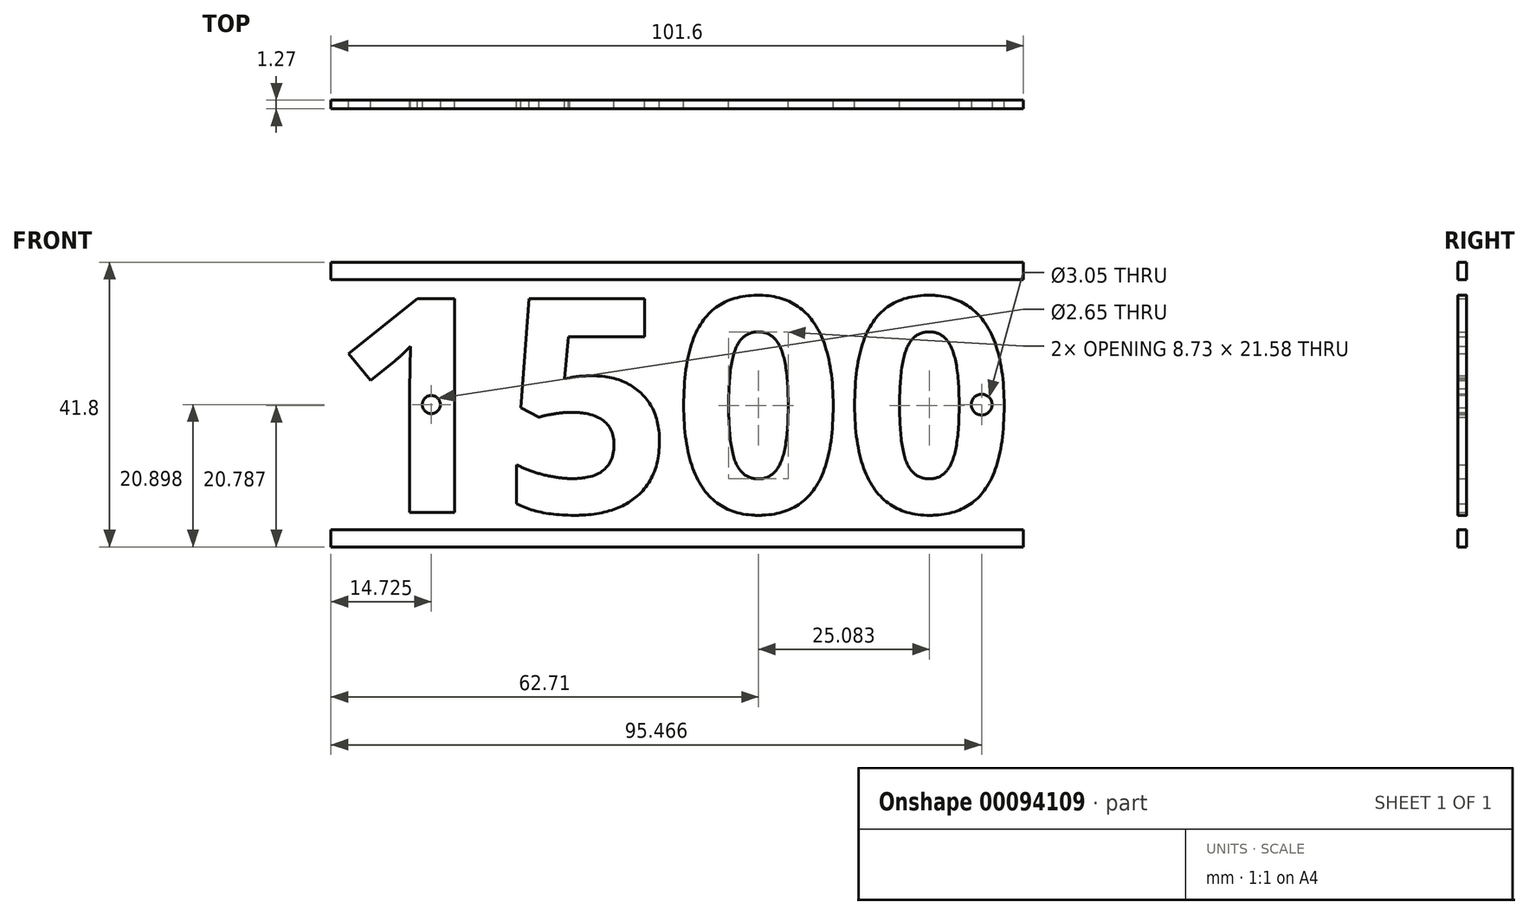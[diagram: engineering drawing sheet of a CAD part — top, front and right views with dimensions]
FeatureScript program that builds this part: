
annotation { "Feature Type Name" : "Feature", "Feature Type Description" : "" }
export const myFeature = defineFeature(function(context is Context, id is Id, definition is map)
    precondition{}
    {
        {
            var Q0;
            Q0=qCreatedBy(makeId("Front.planeOp"),FACE);
            var sketch = newSketch(context, id + "F0", { "sketchPlane" : qUnion([Q0])});
            skText(sketch, "E0", { "text": "1500", "fontName": "OpenSans-Bold.ttf"});
            skLineSegment(sketch, "E1.bottom", {"start": v(0, -2.54) * mm, "end": v(101.6, -2.54) * mm});
            skLineSegment(sketch, "E1.top", {"start": v(0, -5.08) * mm, "end": v(101.6, -5.08) * mm});
            skLineSegment(sketch, "E1.left", {"start": v(0, -2.54) * mm, "end": v(0, -5.08) * mm});
            skLineSegment(sketch, "E1.right", {"start": v(101.6, -2.54) * mm, "end": v(101.6, -5.08) * mm});
            skLineSegment(sketch, "E2.bottom", {"start": v(0, 36.72) * mm, "end": v(101.6, 36.72) * mm});
            skLineSegment(sketch, "E2.top", {"start": v(0, 34.18) * mm, "end": v(101.6, 34.18) * mm});
            skLineSegment(sketch, "E2.left", {"start": v(0, 36.72) * mm, "end": v(0, 34.18) * mm});
            skLineSegment(sketch, "E2.right", {"start": v(101.6, 36.72) * mm, "end": v(101.6, 34.18) * mm});
            skLineSegment(sketch, "E3.bottom", {"start": v(14.13, 34.18) * mm, "end": v(15.4, 34.18) * mm});
            skLineSegment(sketch, "E3.top", {"start": v(14.13, -2.54) * mm, "end": v(15.4, -2.54) * mm});
            skLineSegment(sketch, "E3.left", {"start": v(14.13, 34.18) * mm, "end": v(14.13, -2.54) * mm});
            skLineSegment(sketch, "E3.right", {"start": v(15.4, 34.18) * mm, "end": v(15.4, -2.54) * mm});
            skLineSegment(sketch, "E4.bottom", {"start": v(36.1, 34.18) * mm, "end": v(37.37, 34.18) * mm});
            skLineSegment(sketch, "E4.top", {"start": v(36.1, -2.54) * mm, "end": v(37.37, -2.54) * mm});
            skLineSegment(sketch, "E4.left", {"start": v(36.1, 34.18) * mm, "end": v(36.1, -2.54) * mm});
            skLineSegment(sketch, "E4.right", {"start": v(37.37, 34.18) * mm, "end": v(37.37, -2.54) * mm});
            skLineSegment(sketch, "E5.bottom", {"start": v(62.1, 34.18) * mm, "end": v(63.38, 34.18) * mm});
            skLineSegment(sketch, "E5.top", {"start": v(62.1, -2.54) * mm, "end": v(63.38, -2.54) * mm});
            skLineSegment(sketch, "E5.left", {"start": v(62.1, 34.18) * mm, "end": v(62.1, -2.54) * mm});
            skLineSegment(sketch, "E5.right", {"start": v(63.38, 34.18) * mm, "end": v(63.38, -2.54) * mm});
            skLineSegment(sketch, "E6.bottom", {"start": v(87.42, 34.18) * mm, "end": v(88.69, 34.18) * mm});
            skLineSegment(sketch, "E6.top", {"start": v(87.42, -2.54) * mm, "end": v(88.69, -2.54) * mm});
            skLineSegment(sketch, "E6.left", {"start": v(87.42, 34.18) * mm, "end": v(87.42, -2.54) * mm});
            skLineSegment(sketch, "E6.right", {"start": v(88.69, 34.18) * mm, "end": v(88.69, -2.54) * mm});
            skLineSegment(sketch, "E7", {"start": v(36.1, 29.2) * mm, "end": v(37.37, 29.2) * mm});
            skLineSegment(sketch, "E8", {"start": v(36.1, 2.08) * mm, "end": v(37.37, 2.08) * mm});
            skLineSegment(sketch, "E9", {"start": v(62.1, 2.01) * mm, "end": v(63.38, 2.01) * mm});
            skLineSegment(sketch, "E10", {"start": v(62.1, 29.7) * mm, "end": v(63.38, 29.7) * mm});
            skLineSegment(sketch, "E11", {"start": v(87.42, 2.66) * mm, "end": v(88.69, 2.66) * mm});
            skLineSegment(sketch, "E12", {"start": v(87.42, 27.18) * mm, "end": v(88.69, 27.18) * mm});
            const initialGuessF0  = {"E0": [0, 0, 1, 0, 0.03164]};
            skSetInitialGuess(sketch, initialGuessF0);
            skSolve(sketch);
        }
        {
            var Q0;
            Q0=makeQuery(id+"F0.imprint","IMPRINT",FACE,{"disambiguationData":[TD([[makeQuery(id+"F0.imprint","IMPRINT",EDGE,{"derivedFrom":sQuery(id+"F0.wireOp",EDGE,"E2.bottom")}),-1.0]])]});
            var Q1;
            {var subQ5=sQuery(id+"F0.wireOp",EDGE,"E3.bottom");Q1=makeQuery(id+"F0.imprint","IMPRINT",FACE,{"disambiguationData":[TD([[makeQuery(id+"F0.imprint","IMPRINT",EDGE,{"derivedFrom":subQ5}),-1.0]])]});}
            var Q2;
            {var subQ0=sQuery(id+"F0.wireOp",EDGE,"E3.left");var subQ1=sQuery(id+"F0.wireOp",EDGE,"E0.sketch_text.stroke-0");var subQ2=makeQuery(id+"F0.imprint","INTERSECT",VERTEX,{"derivedFrom":[subQ1,subQ0]});Q2=makeQuery(id+"F0.imprint","IMPRINT",FACE,{"disambiguationData":[TD([[makeQuery(id+"F0.imprint","IMPRINT",EDGE,{"disambiguationData":[TD([[subQ2,1.0]])],"derivedFrom":subQ1}),-1.0]])]});}
            var Q3;
            {var subQ0=sQuery(id+"F0.wireOp",EDGE,"E0.sketch_text.stroke-9");Q3=makeQuery(id+"F0.imprint","IMPRINT",FACE,{"disambiguationData":[TD([[makeQuery(id+"F0.imprint","IMPRINT",EDGE,{"derivedFrom":subQ0}),-1.0]])]});}
            var Q4;
            {var subQ0=sQuery(id+"F0.wireOp",EDGE,"E0.sketch_text.stroke-1");Q4=makeQuery(id+"F0.imprint","IMPRINT",FACE,{"disambiguationData":[TD([[makeQuery(id+"F0.imprint","IMPRINT",EDGE,{"derivedFrom":subQ0}),-1.0]])]});}
            var Q5;
            {var subQ5=sQuery(id+"F0.wireOp",EDGE,"E3.top");Q5=makeQuery(id+"F0.imprint","IMPRINT",FACE,{"disambiguationData":[TD([[makeQuery(id+"F0.imprint","IMPRINT",EDGE,{"derivedFrom":subQ5}),1.0]])]});}
            var Q6;
            Q6=makeQuery(id+"F0.imprint","IMPRINT",FACE,{"disambiguationData":[TD([[makeQuery(id+"F0.imprint","IMPRINT",EDGE,{"derivedFrom":sQuery(id+"F0.wireOp",EDGE,"E1.top")}),1.0]])]});
            var Q7;
            {var subQ5=sQuery(id+"F0.wireOp",EDGE,"E4.top");Q7=makeQuery(id+"F0.imprint","IMPRINT",FACE,{"disambiguationData":[TD([[makeQuery(id+"F0.imprint","IMPRINT",EDGE,{"derivedFrom":subQ5}),1.0]])]});}
            var Q8;
            {var subQ9=sQuery(id+"F0.wireOp",EDGE,"E0.sketch_text.stroke-10");Q8=makeQuery(id+"F0.imprint","IMPRINT",FACE,{"disambiguationData":[TD([[makeQuery(id+"F0.imprint","IMPRINT",EDGE,{"derivedFrom":subQ9}),-1.0]])]});}
            var Q9;
            {var subQ1=sQuery(id+"F0.wireOp",EDGE,"E0.sketch_text.stroke-14");Q9=makeQuery(id+"F0.imprint","IMPRINT",FACE,{"disambiguationData":[TD([[makeQuery(id+"F0.imprint","IMPRINT",EDGE,{"derivedFrom":subQ1}),-1.0]])]});}
            var Q10;
            {var subQ5=sQuery(id+"F0.wireOp",EDGE,"E8");Q10=makeQuery(id+"F0.imprint","IMPRINT",FACE,{"disambiguationData":[TD([[makeQuery(id+"F0.imprint","IMPRINT",EDGE,{"derivedFrom":subQ5}),1.0]])]});}
            var Q11;
            {var subQ5=sQuery(id+"F0.wireOp",EDGE,"E8");Q11=makeQuery(id+"F0.imprint","IMPRINT",FACE,{"disambiguationData":[TD([[makeQuery(id+"F0.imprint","IMPRINT",EDGE,{"derivedFrom":subQ5}),-1.0]])]});}
            var Q12;
            {var subQ0=sQuery(id+"F0.wireOp",EDGE,"E4.right");var subQ1=sQuery(id+"F0.wireOp",EDGE,"E0.sketch_text.stroke-19");var subQ2=makeQuery(id+"F0.imprint","INTERSECT",VERTEX,{"derivedFrom":[subQ1,subQ0]});Q12=makeQuery(id+"F0.imprint","IMPRINT",FACE,{"disambiguationData":[TD([[makeQuery(id+"F0.imprint","IMPRINT",EDGE,{"disambiguationData":[TD([[subQ2,-1.0]])],"derivedFrom":subQ1}),-1.0]])]});}
            var Q13;
            {var subQ10=sQuery(id+"F0.wireOp",EDGE,"E0.sketch_text.stroke-20");Q13=makeQuery(id+"F0.imprint","IMPRINT",FACE,{"disambiguationData":[TD([[makeQuery(id+"F0.imprint","IMPRINT",EDGE,{"derivedFrom":subQ10}),-1.0]])]});}
            var Q14;
            {var subQ5=sQuery(id+"F0.wireOp",EDGE,"E7");Q14=makeQuery(id+"F0.imprint","IMPRINT",FACE,{"disambiguationData":[TD([[makeQuery(id+"F0.imprint","IMPRINT",EDGE,{"derivedFrom":subQ5}),-1.0]])]});}
            var Q15;
            {var subQ5=sQuery(id+"F0.wireOp",EDGE,"E7");Q15=makeQuery(id+"F0.imprint","IMPRINT",FACE,{"disambiguationData":[TD([[makeQuery(id+"F0.imprint","IMPRINT",EDGE,{"derivedFrom":subQ5}),1.0]])]});}
            var Q16;
            {var subQ4=sQuery(id+"F0.wireOp",EDGE,"E0.sketch_text.stroke-25");Q16=makeQuery(id+"F0.imprint","IMPRINT",FACE,{"disambiguationData":[TD([[makeQuery(id+"F0.imprint","IMPRINT",EDGE,{"derivedFrom":subQ4}),-1.0]])]});}
            var Q17;
            {var subQ7=sQuery(id+"F0.wireOp",EDGE,"E0.sketch_text.stroke-33");Q17=makeQuery(id+"F0.imprint","IMPRINT",FACE,{"disambiguationData":[TD([[makeQuery(id+"F0.imprint","IMPRINT",EDGE,{"derivedFrom":subQ7}),-1.0]])]});}
            var Q18;
            {var subQ8=sQuery(id+"F0.wireOp",EDGE,"E0.sketch_text.stroke-30");Q18=makeQuery(id+"F0.imprint","IMPRINT",FACE,{"disambiguationData":[TD([[makeQuery(id+"F0.imprint","IMPRINT",EDGE,{"derivedFrom":subQ8}),-1.0]])]});}
            var Q19;
            {var subQ7=sQuery(id+"F0.wireOp",EDGE,"E0.sketch_text.stroke-49");Q19=makeQuery(id+"F0.imprint","IMPRINT",FACE,{"disambiguationData":[TD([[makeQuery(id+"F0.imprint","IMPRINT",EDGE,{"derivedFrom":subQ7}),-1.0]])]});}
            var Q20;
            {var subQ7=sQuery(id+"F0.wireOp",EDGE,"E0.sketch_text.stroke-46");Q20=makeQuery(id+"F0.imprint","IMPRINT",FACE,{"disambiguationData":[TD([[makeQuery(id+"F0.imprint","IMPRINT",EDGE,{"derivedFrom":subQ7}),-1.0]])]});}
            var Q21;
            {var subQ1=sQuery(id+"F0.wireOp",EDGE,"E6.bottom");Q21=makeQuery(id+"F0.imprint","IMPRINT",FACE,{"disambiguationData":[TD([[makeQuery(id+"F0.imprint","IMPRINT",EDGE,{"derivedFrom":subQ1}),-1.0]])]});}
            var Q22;
            {var subQ1=sQuery(id+"F0.wireOp",EDGE,"E5.bottom");Q22=makeQuery(id+"F0.imprint","IMPRINT",FACE,{"disambiguationData":[TD([[makeQuery(id+"F0.imprint","IMPRINT",EDGE,{"derivedFrom":subQ1}),-1.0]])]});}
            var Q23;
            {var subQ0=sQuery(id+"F0.wireOp",EDGE,"E10");Q23=makeQuery(id+"F0.imprint","IMPRINT",FACE,{"disambiguationData":[TD([[makeQuery(id+"F0.imprint","IMPRINT",EDGE,{"derivedFrom":subQ0}),1.0]])]});}
            var Q24;
            {var subQ0=sQuery(id+"F0.wireOp",EDGE,"E10");Q24=makeQuery(id+"F0.imprint","IMPRINT",FACE,{"disambiguationData":[TD([[makeQuery(id+"F0.imprint","IMPRINT",EDGE,{"derivedFrom":subQ0}),-1.0]])]});}
            var Q25;
            {var subQ0=sQuery(id+"F0.wireOp",EDGE,"E9");Q25=makeQuery(id+"F0.imprint","IMPRINT",FACE,{"disambiguationData":[TD([[makeQuery(id+"F0.imprint","IMPRINT",EDGE,{"derivedFrom":subQ0}),1.0]])]});}
            var Q26;
            {var subQ0=sQuery(id+"F0.wireOp",EDGE,"E9");Q26=makeQuery(id+"F0.imprint","IMPRINT",FACE,{"disambiguationData":[TD([[makeQuery(id+"F0.imprint","IMPRINT",EDGE,{"derivedFrom":subQ0}),-1.0]])]});}
            var Q27;
            {var subQ0=sQuery(id+"F0.wireOp",EDGE,"E5.top");Q27=makeQuery(id+"F0.imprint","IMPRINT",FACE,{"disambiguationData":[TD([[makeQuery(id+"F0.imprint","IMPRINT",EDGE,{"derivedFrom":subQ0}),1.0]])]});}
            var Q28;
            {var subQ1=sQuery(id+"F0.wireOp",EDGE,"E6.top");Q28=makeQuery(id+"F0.imprint","IMPRINT",FACE,{"disambiguationData":[TD([[makeQuery(id+"F0.imprint","IMPRINT",EDGE,{"derivedFrom":subQ1}),1.0]])]});}
            var Q29;
            {var subQ0=sQuery(id+"F0.wireOp",EDGE,"E11");Q29=makeQuery(id+"F0.imprint","IMPRINT",FACE,{"disambiguationData":[TD([[makeQuery(id+"F0.imprint","IMPRINT",EDGE,{"derivedFrom":subQ0}),-1.0]])]});}
            var Q30;
            {var subQ0=sQuery(id+"F0.wireOp",EDGE,"E11");Q30=makeQuery(id+"F0.imprint","IMPRINT",FACE,{"disambiguationData":[TD([[makeQuery(id+"F0.imprint","IMPRINT",EDGE,{"derivedFrom":subQ0}),1.0]])]});}
            var Q31;
            {var subQ0=sQuery(id+"F0.wireOp",EDGE,"E12");Q31=makeQuery(id+"F0.imprint","IMPRINT",FACE,{"disambiguationData":[TD([[makeQuery(id+"F0.imprint","IMPRINT",EDGE,{"derivedFrom":subQ0}),1.0]])]});}
            var Q32;
            {var subQ5=sQuery(id+"F0.wireOp",EDGE,"E4.bottom");Q32=makeQuery(id+"F0.imprint","IMPRINT",FACE,{"disambiguationData":[TD([[makeQuery(id+"F0.imprint","IMPRINT",EDGE,{"derivedFrom":subQ5}),-1.0]])]});}
            var Q33;
            {var subQ0=sQuery(id+"F0.wireOp",EDGE,"E12");Q33=makeQuery(id+"F0.imprint","IMPRINT",FACE,{"disambiguationData":[TD([[makeQuery(id+"F0.imprint","IMPRINT",EDGE,{"derivedFrom":subQ0}),-1.0]])]});}
            extrude(context, id + "F1", {"entities" : qUnion([Q0, Q1, Q2, Q3, Q4, Q5, Q6, Q7, Q8, Q9, Q10, Q11, Q12, Q13, Q14, Q15, Q16, Q17, Q18, Q19, Q20, Q21, Q22, Q23, Q24, Q25, Q26, Q27, Q28, Q29, Q30, Q31, Q32, Q33]), "depth" : 1.27 * mm});
        }
        {
            var Q0;
            Q0=makeQuery(id+"F1.opExtrude","CAP_FACE",FACE,{"disambiguationData":[OSD([sQuery(id+"F0.wireOp",EDGE,"E0.sketch_text.stroke-0"),sQuery(id+"F0.wireOp",EDGE,"E0.sketch_text.stroke-1"),sQuery(id+"F0.wireOp",EDGE,"E0.sketch_text.stroke-2"),sQuery(id+"F0.wireOp",EDGE,"E0.sketch_text.stroke-3"),sQuery(id+"F0.wireOp",EDGE,"E0.sketch_text.stroke-4"),sQuery(id+"F0.wireOp",EDGE,"E0.sketch_text.stroke-5"),sQuery(id+"F0.wireOp",EDGE,"E0.sketch_text.stroke-6"),sQuery(id+"F0.wireOp",EDGE,"E0.sketch_text.stroke-7"),sQuery(id+"F0.wireOp",EDGE,"E0.sketch_text.stroke-8"),sQuery(id+"F0.wireOp",EDGE,"E0.sketch_text.stroke-9"),sQuery(id+"F0.wireOp",EDGE,"E0.sketch_text.stroke-10"),sQuery(id+"F0.wireOp",EDGE,"E0.sketch_text.stroke-11"),sQuery(id+"F0.wireOp",EDGE,"E0.sketch_text.stroke-12"),sQuery(id+"F0.wireOp",EDGE,"E0.sketch_text.stroke-13"),sQuery(id+"F0.wireOp",EDGE,"E0.sketch_text.stroke-14"),sQuery(id+"F0.wireOp",EDGE,"E0.sketch_text.stroke-15"),sQuery(id+"F0.wireOp",EDGE,"E0.sketch_text.stroke-16"),sQuery(id+"F0.wireOp",EDGE,"E0.sketch_text.stroke-17"),sQuery(id+"F0.wireOp",EDGE,"E0.sketch_text.stroke-18"),sQuery(id+"F0.wireOp",EDGE,"E0.sketch_text.stroke-19"),sQuery(id+"F0.wireOp",EDGE,"E0.sketch_text.stroke-20"),sQuery(id+"F0.wireOp",EDGE,"E0.sketch_text.stroke-21"),sQuery(id+"F0.wireOp",EDGE,"E0.sketch_text.stroke-22"),sQuery(id+"F0.wireOp",EDGE,"E0.sketch_text.stroke-23"),sQuery(id+"F0.wireOp",EDGE,"E0.sketch_text.stroke-24"),sQuery(id+"F0.wireOp",EDGE,"E0.sketch_text.stroke-25"),sQuery(id+"F0.wireOp",EDGE,"E0.sketch_text.stroke-26"),sQuery(id+"F0.wireOp",EDGE,"E0.sketch_text.stroke-27"),sQuery(id+"F0.wireOp",EDGE,"E0.sketch_text.stroke-28"),sQuery(id+"F0.wireOp",EDGE,"E0.sketch_text.stroke-29"),sQuery(id+"F0.wireOp",EDGE,"E0.sketch_text.stroke-30"),sQuery(id+"F0.wireOp",EDGE,"E0.sketch_text.stroke-31"),sQuery(id+"F0.wireOp",EDGE,"E0.sketch_text.stroke-32"),sQuery(id+"F0.wireOp",EDGE,"E0.sketch_text.stroke-33"),sQuery(id+"F0.wireOp",EDGE,"E0.sketch_text.stroke-34"),sQuery(id+"F0.wireOp",EDGE,"E0.sketch_text.stroke-35"),sQuery(id+"F0.wireOp",EDGE,"E0.sketch_text.stroke-36"),sQuery(id+"F0.wireOp",EDGE,"E0.sketch_text.stroke-37"),sQuery(id+"F0.wireOp",EDGE,"E0.sketch_text.stroke-38"),sQuery(id+"F0.wireOp",EDGE,"E0.sketch_text.stroke-39"),sQuery(id+"F0.wireOp",EDGE,"E0.sketch_text.stroke-40"),sQuery(id+"F0.wireOp",EDGE,"E0.sketch_text.stroke-41"),sQuery(id+"F0.wireOp",EDGE,"E0.sketch_text.stroke-42"),sQuery(id+"F0.wireOp",EDGE,"E0.sketch_text.stroke-43"),sQuery(id+"F0.wireOp",EDGE,"E0.sketch_text.stroke-44"),sQuery(id+"F0.wireOp",EDGE,"E0.sketch_text.stroke-45"),sQuery(id+"F0.wireOp",EDGE,"E0.sketch_text.stroke-46"),sQuery(id+"F0.wireOp",EDGE,"E0.sketch_text.stroke-47"),sQuery(id+"F0.wireOp",EDGE,"E0.sketch_text.stroke-48"),sQuery(id+"F0.wireOp",EDGE,"E0.sketch_text.stroke-49"),sQuery(id+"F0.wireOp",EDGE,"E0.sketch_text.stroke-50"),sQuery(id+"F0.wireOp",EDGE,"E0.sketch_text.stroke-51"),sQuery(id+"F0.wireOp",EDGE,"E0.sketch_text.stroke-52"),sQuery(id+"F0.wireOp",EDGE,"E0.sketch_text.stroke-53"),sQuery(id+"F0.wireOp",EDGE,"E0.sketch_text.stroke-54"),sQuery(id+"F0.wireOp",EDGE,"E0.sketch_text.stroke-55"),sQuery(id+"F0.wireOp",EDGE,"E0.sketch_text.stroke-56"),sQuery(id+"F0.wireOp",EDGE,"E0.sketch_text.stroke-57"),sQuery(id+"F0.wireOp",EDGE,"E0.sketch_text.stroke-58"),sQuery(id+"F0.wireOp",EDGE,"E0.sketch_text.stroke-59"),sQuery(id+"F0.wireOp",EDGE,"E0.sketch_text.stroke-60"),sQuery(id+"F0.wireOp",EDGE,"E0.sketch_text.stroke-61"),sQuery(id+"F0.wireOp",EDGE,"E1.bottom"),sQuery(id+"F0.wireOp",EDGE,"E1.top"),sQuery(id+"F0.wireOp",EDGE,"E1.left"),sQuery(id+"F0.wireOp",EDGE,"E1.right"),sQuery(id+"F0.wireOp",EDGE,"E2.bottom"),sQuery(id+"F0.wireOp",EDGE,"E2.top"),sQuery(id+"F0.wireOp",EDGE,"E2.left"),sQuery(id+"F0.wireOp",EDGE,"E2.right"),sQuery(id+"F0.wireOp",EDGE,"E3.left"),sQuery(id+"F0.wireOp",EDGE,"E3.right"),sQuery(id+"F0.wireOp",EDGE,"E4.left"),sQuery(id+"F0.wireOp",EDGE,"E4.right"),sQuery(id+"F0.wireOp",EDGE,"E5.left"),sQuery(id+"F0.wireOp",EDGE,"E5.right"),sQuery(id+"F0.wireOp",EDGE,"E6.left"),sQuery(id+"F0.wireOp",EDGE,"E6.right")])],"isStart":false});
            var sketch = newSketch(context, id + "F2", { "sketchPlane" : qUnion([Q0])});
            skCircle(sketch, "E13", {"center": v(14.73, 15.82) * mm, "radius": 1.33 * mm});
            skCircle(sketch, "E14", {"center": v(95.47, 15.82) * mm, "radius": 1.53 * mm});
            skLineSegment(sketch, "E15", {"start": v(95.47, 36.72) * mm, "end": v(95.47, -5.08) * mm, "construction": true});
            skLineSegment(sketch, "E16", {"start": v(14.73, 36.72) * mm, "end": v(14.73, -5.08) * mm, "construction": true});
            skSolve(sketch);
        }
        {
            var Q0;
            Q0=makeQuery(id+"F2.imprint","IMPRINT",FACE,{"disambiguationData":[TD([[makeQuery(id+"F2.imprint","IMPRINT",EDGE,{"derivedFrom":sQuery(id+"F2.wireOp",EDGE,"E13")}),1.0]])]});
            var Q1;
            Q1=makeQuery(id+"F2.imprint","IMPRINT",FACE,{"disambiguationData":[TD([[makeQuery(id+"F2.imprint","IMPRINT",EDGE,{"derivedFrom":sQuery(id+"F2.wireOp",EDGE,"E14")}),1.0]])]});
            extrude(context, id + "F3", {"entities" : qUnion([Q0, Q1]), "operationType" : NewBodyOperationType.REMOVE, "oppositeDirection" : true, "depth" : 25.4 * mm});
        }
    });
